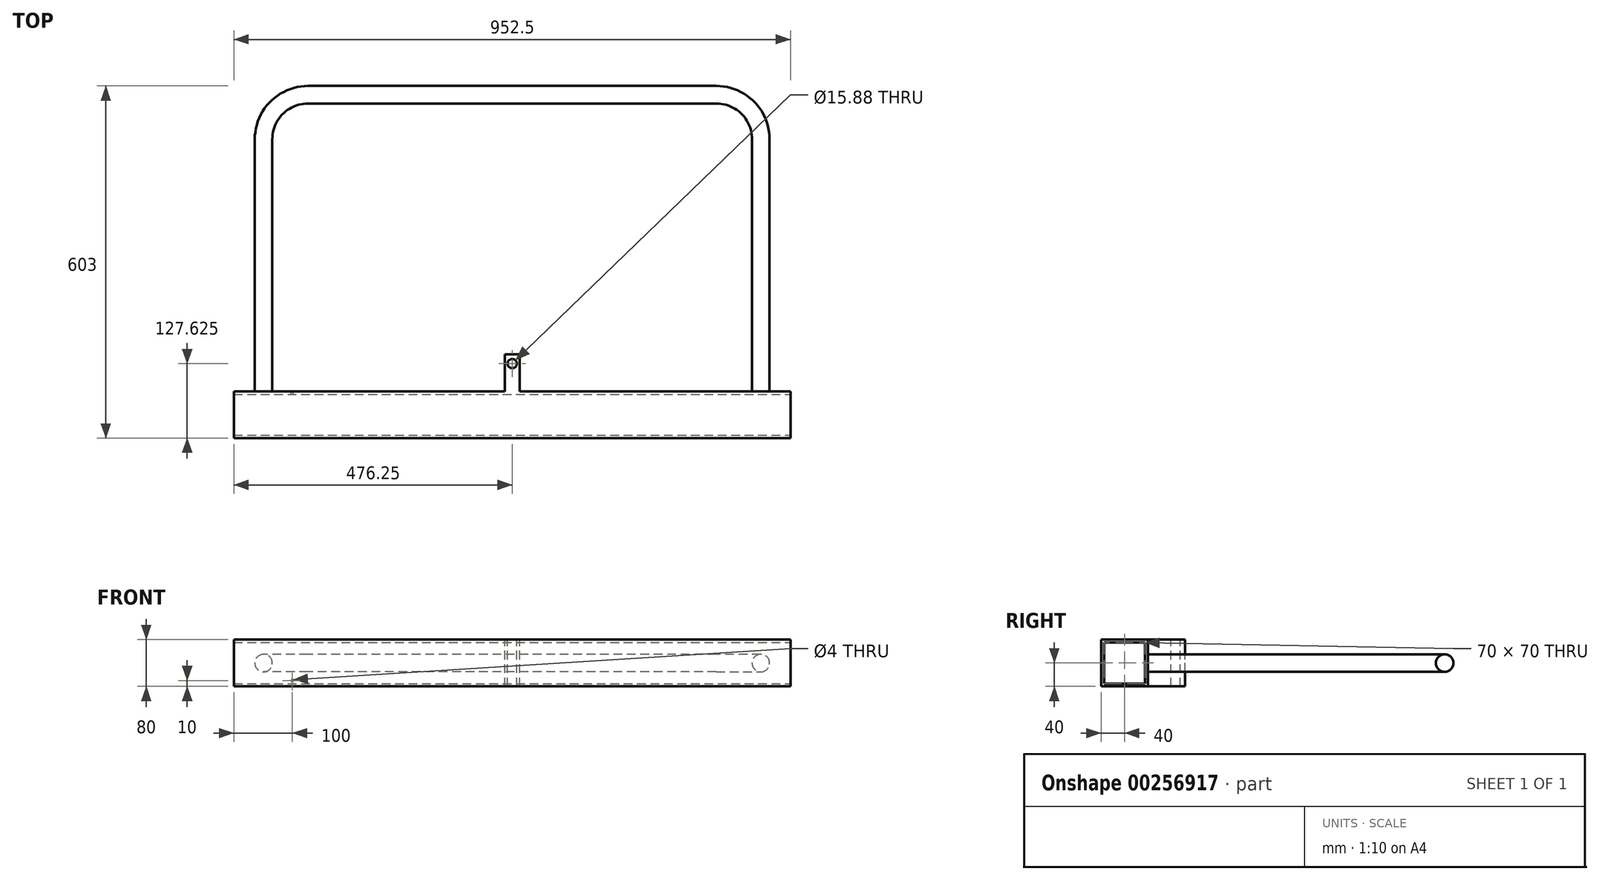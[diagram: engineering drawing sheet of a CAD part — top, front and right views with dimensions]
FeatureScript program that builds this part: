
annotation { "Feature Type Name" : "Feature", "Feature Type Description" : "" }
export const myFeature = defineFeature(function(context is Context, id is Id, definition is map)
    precondition{}
    {
        {
            var Q0;
            Q0=qCreatedBy(makeId("Right.planeOp"),FACE);
            var sketch = newSketch(context, id + "F0", { "sketchPlane" : qUnion([Q0])});
            skLineSegment(sketch, "E0.bottom", {"start": v(0, 0) * mm, "end": v(-80, 0) * mm});
            skLineSegment(sketch, "E0.top", {"start": v(0, 80) * mm, "end": v(-80, 80) * mm});
            skLineSegment(sketch, "E0.left", {"start": v(0, 0) * mm, "end": v(0, 80) * mm});
            skLineSegment(sketch, "E0.right", {"start": v(-80, 0) * mm, "end": v(-80, 80) * mm});
            skLineSegment(sketch, "E1.0", {"start": v(-5, 75) * mm, "end": v(-75, 75) * mm});
            skLineSegment(sketch, "E1.1", {"start": v(-5, 5) * mm, "end": v(-5, 75) * mm});
            skLineSegment(sketch, "E1.2", {"start": v(-5, 5) * mm, "end": v(-75, 5) * mm});
            skLineSegment(sketch, "E1.3", {"start": v(-75, 5) * mm, "end": v(-75, 75) * mm});
            skSolve(sketch);
        }
        {
            var Q0;
            Q0=makeQuery(id+"F0.imprint","IMPRINT",FACE,{"disambiguationData":[TD([[makeQuery(id+"F0.imprint","IMPRINT",EDGE,{"derivedFrom":sQuery(id+"F0.wireOp",EDGE,"E0.bottom")}),-1.0]])]});
            extrude(context, id + "F1", {"entities" : qUnion([Q0]), "oppositeDirection" : true, "depth" : 952.5 * mm});
        }
        {
            var Q0;
            Q0=makeQuery(id+"F1.opExtrude","SWEPT_FACE",FACE,{"disambiguationData":[OSD([sQuery(id+"F0.wireOp",EDGE,"E0.top")])]});
            var Q1;
            Q1=makeQuery(id+"F1.opExtrude","SWEPT_FACE",FACE,{"disambiguationData":[OSD([sQuery(id+"F0.wireOp",EDGE,"E0.bottom")])]});
            cPlane(context, id + "F2", {"entities" : qUnion([Q0, Q1]), "cplaneType" : CPlaneType.MID_PLANE, "offset" : 25.4 * mm, "width" : 152.4 * mm, "height" : 152.4 * mm});
        }
        {
            var Q0;
            Q0=qCreatedBy(id+"F2.planeOp",FACE);
            var sketch = newSketch(context, id + "F3", { "sketchPlane" : qUnion([Q0])});
            skLineSegment(sketch, "E2", {"start": v(-50.8, 0) * mm, "end": v(-50.8, 431.8) * mm});
            skLineSegment(sketch, "E3", {"start": v(-127, 508) * mm, "end": v(-825.5, 508) * mm});
            skLineSegment(sketch, "E4", {"start": v(-901.7, 431.8) * mm, "end": v(-901.7, 0) * mm});
            skPoint(sketch, "E5.visualSharp", {"position": v(-901.7, 508) * mm});
            skArc(sketch, "E5.filletArc", {"start": v(-825.5, 508) * mm, "mid": v(-879.38, 485.68) * mm, "end": v(-901.7, 431.8) * mm});
            skPoint(sketch, "E6.visualSharp", {"position": v(-50.8, 508) * mm});
            skArc(sketch, "E6.filletArc", {"start": v(-50.8, 431.8) * mm, "mid": v(-73.12, 485.68) * mm, "end": v(-127, 508) * mm});
            skSolve(sketch);
        }
        {
            var Q0;
            Q0=makeQuery(id+"F1.opExtrude","SWEPT_FACE",FACE,{"disambiguationData":[OSD([sQuery(id+"F0.wireOp",EDGE,"E0.left")])]});
            var sketch = newSketch(context, id + "F4", { "sketchPlane" : qUnion([Q0])});
            skCircle(sketch, "E7", {"center": v(50.8, 40) * mm, "radius": 15 * mm});
            skPoint(sketch, "E7.centerSnap0", {"position": v(0, 40) * mm});
            skCircle(sketch, "E8", {"center": v(901.7, 40) * mm, "radius": 15 * mm});
            skPoint(sketch, "E8.centerSnap0", {"position": v(952.5, 40) * mm});
            skSolve(sketch);
        }
        {
            var Q0;
            Q0=makeQuery(id+"F4.imprint","IMPRINT",FACE,{"disambiguationData":[TD([[makeQuery(id+"F4.imprint","IMPRINT",EDGE,{"derivedFrom":sQuery(id+"F4.wireOp",EDGE,"E7")}),1.0]])]});
            var Q1;
            Q1 = qSketchRegion(id + "F3", true);
            var Q2;
            Q2=sQuery(id+"F3.wireOp",EDGE,"E2");
            var Q3;
            Q3=sQuery(id+"F3.wireOp",EDGE,"E6.filletArc");
            var Q4;
            Q4=sQuery(id+"F3.wireOp",EDGE,"E3");
            var Q5;
            Q5=sQuery(id+"F3.wireOp",EDGE,"E5.filletArc");
            var Q6;
            Q6=sQuery(id+"F3.wireOp",EDGE,"E4");
            sweep(context, id + "F5", {"operationType" : NewBodyOperationType.ADD, "profiles" : qUnion([Q0, Q1]), "path" : qUnion([Q2, Q3, Q4, Q5, Q6])});
        }
        {
            var Q0;
            Q0=makeQuery(id+"F1.opExtrude","CAP_FACE",FACE,{"disambiguationData":[OSD([sQuery(id+"F0.wireOp",EDGE,"E0.bottom"),sQuery(id+"F0.wireOp",EDGE,"E0.top"),sQuery(id+"F0.wireOp",EDGE,"E0.left"),sQuery(id+"F0.wireOp",EDGE,"E0.right"),sQuery(id+"F0.wireOp",EDGE,"E1.0"),sQuery(id+"F0.wireOp",EDGE,"E1.1"),sQuery(id+"F0.wireOp",EDGE,"E1.2"),sQuery(id+"F0.wireOp",EDGE,"E1.3")])],"isStart":true});
            var Q1;
            Q1=makeQuery(id+"F1.opExtrude","CAP_FACE",FACE,{"disambiguationData":[OSD([sQuery(id+"F0.wireOp",EDGE,"E0.bottom"),sQuery(id+"F0.wireOp",EDGE,"E0.top"),sQuery(id+"F0.wireOp",EDGE,"E0.left"),sQuery(id+"F0.wireOp",EDGE,"E0.right"),sQuery(id+"F0.wireOp",EDGE,"E1.0"),sQuery(id+"F0.wireOp",EDGE,"E1.1"),sQuery(id+"F0.wireOp",EDGE,"E1.2"),sQuery(id+"F0.wireOp",EDGE,"E1.3")])],"isStart":false});
            cPlane(context, id + "F6", {"entities" : qUnion([Q0, Q1]), "cplaneType" : CPlaneType.MID_PLANE, "offset" : 25.4 * mm, "width" : 152.4 * mm, "height" : 152.4 * mm});
        }
        {
            var Q0;
            Q0=qCreatedBy(id+"F6.planeOp",FACE);
            var sketch = newSketch(context, id + "F7", { "sketchPlane" : qUnion([Q0])});
            skLineSegment(sketch, "E9.bottom", {"start": v(0, 0) * mm, "end": v(63.5, 0) * mm});
            skLineSegment(sketch, "E9.top", {"start": v(0, 80) * mm, "end": v(63.5, 80) * mm});
            skLineSegment(sketch, "E9.left", {"start": v(0, 0) * mm, "end": v(0, 80) * mm});
            skLineSegment(sketch, "E9.right", {"start": v(63.5, 0) * mm, "end": v(63.5, 80) * mm});
            skSolve(sketch);
        }
        {
            var Q0;
            Q0=makeQuery(id+"F7.imprint","IMPRINT",FACE,{"disambiguationData":[TD([[makeQuery(id+"F7.imprint","IMPRINT",EDGE,{"derivedFrom":sQuery(id+"F7.wireOp",EDGE,"E9.bottom")}),1.0]])]});
            extrude(context, id + "F8", {"entities" : qUnion([Q0]), "operationType" : NewBodyOperationType.ADD, "endBound" : BoundingType.SYMMETRIC, "depth" : 25 * mm});
        }
        {
            var Q0;
            Q0=makeQuery(id+"F8.boolean.opBoolean","MERGE",FACE,{"derivedFrom":[makeQuery(id+"F1.opExtrude","SWEPT_FACE",FACE,{"disambiguationData":[OSD([sQuery(id+"F0.wireOp",EDGE,"E0.top")])]}),makeQuery(id+"F8.opExtrude","SWEPT_FACE",FACE,{"disambiguationData":[OSD([sQuery(id+"F7.wireOp",EDGE,"E9.top")])]})]});
            var sketch = newSketch(context, id + "F9", { "sketchPlane" : qUnion([Q0])});
            skCircle(sketch, "E10", {"center": v(-476.25, 47.63) * mm, "radius": 7.94 * mm});
            skPoint(sketch, "E10.centerSnap0", {"position": v(-476.25, 63.5) * mm});
            skSolve(sketch);
        }
        {
            var Q0;
            Q0=makeQuery(id+"F9.imprint","IMPRINT",FACE,{"disambiguationData":[TD([[makeQuery(id+"F9.imprint","IMPRINT",EDGE,{"derivedFrom":sQuery(id+"F9.wireOp",EDGE,"E10")}),1.0]])]});
            extrude(context, id + "F10", {"entities" : qUnion([Q0]), "operationType" : NewBodyOperationType.REMOVE, "endBound" : BoundingType.THROUGH_ALL, "oppositeDirection" : true, "depth" : 25.4 * mm});
        }
        {
            var Q0;
            {var subQ1=sQuery(id+"F0.wireOp",EDGE,"E0.left");Q0=makeQuery(id+"F8.boolean.opBoolean","SPLIT",FACE,{"disambiguationData":[TD([makeQuery(id+"F5.opSweep","SWEPT_FACE",FACE,{"disambiguationData":[OSD([sQuery(id+"F3.wireOp",EDGE,"E4"),sQuery(id+"F4.wireOp",EDGE,"E7")])]})])],"derivedFrom":makeQuery(id+"F1.opExtrude","SWEPT_FACE",FACE,{"disambiguationData":[OSD([subQ1])]})});}
            var sketch = newSketch(context, id + "F11", { "sketchPlane" : qUnion([Q0])});
            skCircle(sketch, "E11", {"center": v(852.5, 10) * mm, "radius": 2 * mm});
            skSolve(sketch);
        }
        {
            var Q0;
            Q0 = qSketchRegion(id + "F11", true);
            extrude(context, id + "F12", {"entities" : qUnion([Q0]), "operationType" : NewBodyOperationType.REMOVE, "endBound" : BoundingType.UP_TO_NEXT, "oppositeDirection" : true, "depth" : 25.4 * mm});
        }
    });
